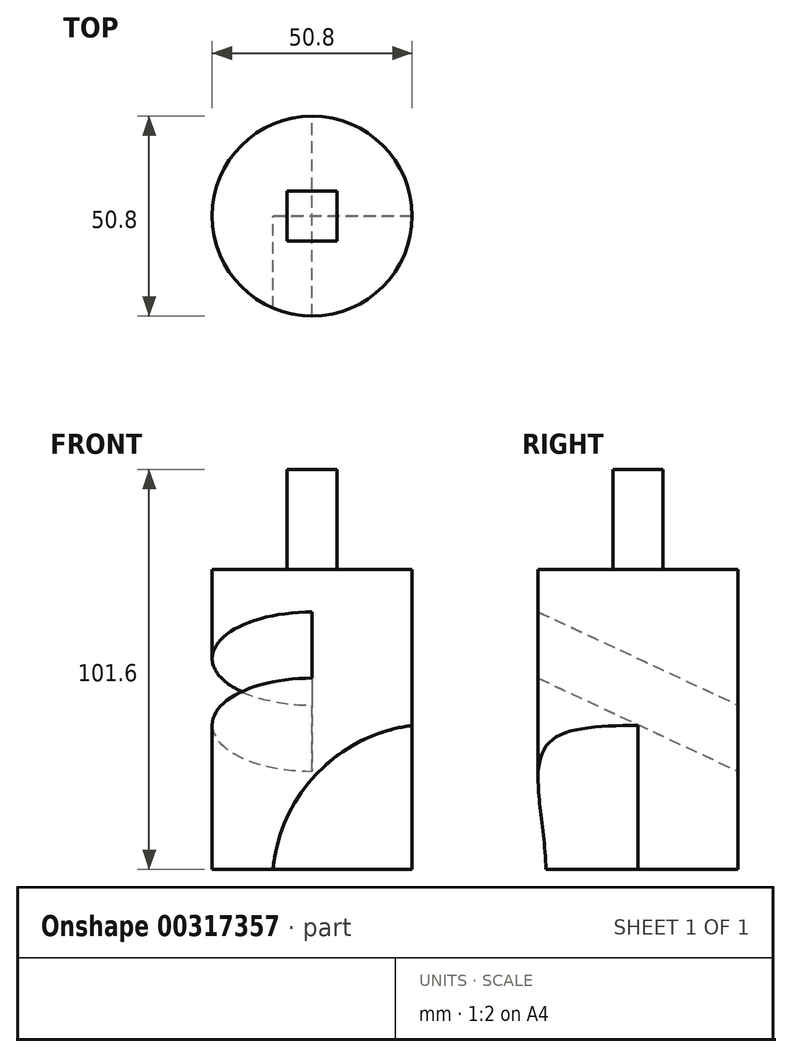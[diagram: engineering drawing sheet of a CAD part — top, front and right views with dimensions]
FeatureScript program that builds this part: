
annotation { "Feature Type Name" : "Feature", "Feature Type Description" : "" }
export const myFeature = defineFeature(function(context is Context, id is Id, definition is map)
    precondition{}
    {
        {
            var Q0;
            Q0=qCreatedBy(makeId("Front.planeOp"),FACE);
            var sketch = newSketch(context, id + "F0", { "sketchPlane" : qUnion([Q0])});
            skLineSegment(sketch, "E0.bottom", {"start": v(0, 30.48) * mm, "end": v(25.4, 30.48) * mm});
            skLineSegment(sketch, "E0.top", {"start": v(0, -45.72) * mm, "end": v(25.4, -45.72) * mm});
            skLineSegment(sketch, "E0.left", {"start": v(0, 30.48) * mm, "end": v(0, -45.72) * mm});
            skLineSegment(sketch, "E0.right", {"start": v(25.4, 30.48) * mm, "end": v(25.4, -45.72) * mm});
            skSolve(sketch);
        }
        {
            var Q0;
            Q0=makeQuery(id+"F0.imprint","IMPRINT",FACE,{"disambiguationData":[TD([[makeQuery(id+"F0.imprint","IMPRINT",EDGE,{"derivedFrom":sQuery(id+"F0.wireOp",EDGE,"E0.bottom")}),-1.0]])]});
            var Q1;
            Q1=sQuery(id+"F0.wireOp",EDGE,"E0.left");
            revolve(context, id + "F1", {"entities" : qUnion([Q0]), "axis" : qUnion([Q1]), "revolveType" : RevolveType.FULL});
        }
        {
            var Q0;
            Q0=qCreatedBy(makeId("Right.planeOp"),FACE);
            var sketch = newSketch(context, id + "F2", { "sketchPlane" : qUnion([Q0])});
            skLineSegment(sketch, "E1", {"start": v(-37.6, 25.4) * mm, "end": v(45.27, -13.25) * mm});
            skLineSegment(sketch, "E2", {"start": v(0, 30.54) * mm, "end": v(-44.22, 30.54) * mm});
            skLineSegment(sketch, "E3.0", {"start": v(-44.05, 11.59) * mm, "end": v(38.83, -27.06) * mm});
            skLineSegment(sketch, "E4", {"start": v(-44.05, 11.59) * mm, "end": v(-37.6, 25.4) * mm});
            skLineSegment(sketch, "E5", {"start": v(38.83, -27.06) * mm, "end": v(45.27, -13.25) * mm});
            skSolve(sketch);
        }
        {
            var Q0;
            Q0=makeQuery(id+"F2.imprint","IMPRINT",FACE,{"disambiguationData":[TD([[makeQuery(id+"F2.imprint","IMPRINT",EDGE,{"derivedFrom":sQuery(id+"F2.wireOp",EDGE,"E1")}),-1.0]])]});
            extrude(context, id + "F3", {"entities" : qUnion([Q0]), "operationType" : NewBodyOperationType.REMOVE, "oppositeDirection" : true, "depth" : 58.42 * mm});
        }
        {
            var Q0;
            Q0=makeQuery(id+"F1.opRevolve","SWEPT_FACE",FACE,{"disambiguationData":[OSD([sQuery(id+"F0.wireOp",EDGE,"E0.bottom")])]});
            var sketch = newSketch(context, id + "F4", { "sketchPlane" : qUnion([Q0])});
            skLineSegment(sketch, "E6.bottom", {"start": v(6.35, 6.35) * mm, "end": v(-6.35, 6.35) * mm});
            skLineSegment(sketch, "E6.top", {"start": v(6.35, -6.35) * mm, "end": v(-6.35, -6.35) * mm});
            skLineSegment(sketch, "E6.left", {"start": v(6.35, 6.35) * mm, "end": v(6.35, -6.35) * mm});
            skLineSegment(sketch, "E6.right", {"start": v(-6.35, 6.35) * mm, "end": v(-6.35, -6.35) * mm});
            skPoint(sketch, "E6.middle", {"position": v(0, 0) * mm});
            skSolve(sketch);
        }
        {
            var Q0;
            Q0=makeQuery(id+"F4.imprint","IMPRINT",FACE,{"disambiguationData":[TD([[makeQuery(id+"F4.imprint","IMPRINT",EDGE,{"derivedFrom":sQuery(id+"F4.wireOp",EDGE,"E6.bottom")}),1.0]])]});
            extrude(context, id + "F5", {"entities" : qUnion([Q0]), "operationType" : NewBodyOperationType.ADD, "depth" : 25.4 * mm});
        }
        {
            var Q0;
            Q0=qCreatedBy(makeId("Front.planeOp"),FACE);
            var sketch = newSketch(context, id + "F6", { "sketchPlane" : qUnion([Q0])});
            skCircle(sketch, "E7", {"center": v(30.54, -49.47) * mm, "radius": 40.64 * mm});
            skSolve(sketch);
        }
        {
            var Q0;
            Q0 = qSketchRegion(id + "F6", true);
            extrude(context, id + "F7", {"entities" : qUnion([Q0]), "operationType" : NewBodyOperationType.REMOVE, "depth" : 87.88 * mm});
        }
    });
